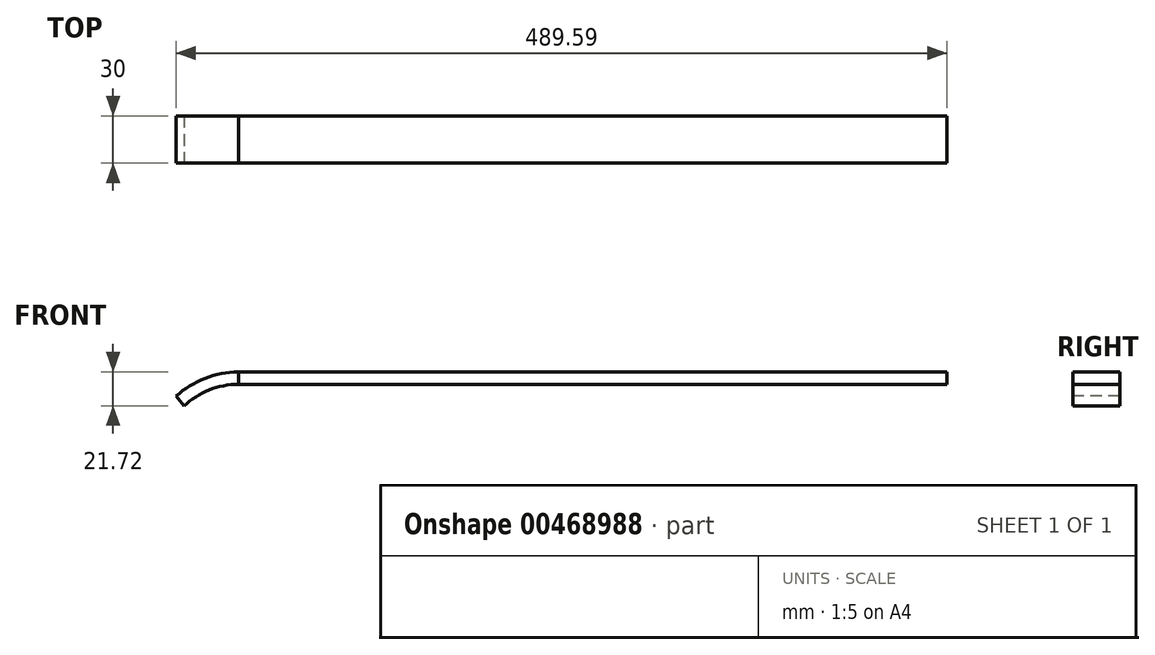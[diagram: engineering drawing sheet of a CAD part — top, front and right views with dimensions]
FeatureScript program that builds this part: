
annotation { "Feature Type Name" : "Feature", "Feature Type Description" : "" }
export const myFeature = defineFeature(function(context is Context, id is Id, definition is map)
    precondition{}
    {
        {
            var Q0;
            Q0=qCreatedBy(makeId("Top.planeOp"),FACE);
            var sketch = newSketch(context, id + "F0", { "sketchPlane" : qUnion([Q0])});
            skLineSegment(sketch, "E0.bottom", {"start": v(0, 0) * mm, "end": v(-450, 0) * mm});
            skLineSegment(sketch, "E0.top", {"start": v(0, -30) * mm, "end": v(-450, -30) * mm});
            skLineSegment(sketch, "E0.left", {"start": v(0, 0) * mm, "end": v(0, -30) * mm});
            skLineSegment(sketch, "E0.right", {"start": v(-450, 0) * mm, "end": v(-450, -30) * mm});
            skSolve(sketch);
        }
        {
            var Q0;
            Q0=makeQuery(id+"F0.imprint","IMPRINT",FACE,{"disambiguationData":[TD([[makeQuery(id+"F0.imprint","IMPRINT",EDGE,{"derivedFrom":sQuery(id+"F0.wireOp",EDGE,"E0.bottom")}),1.0]])]});
            extrude(context, id + "F1", {"entities" : qUnion([Q0]), "depth" : 8 * mm, "offsetDistance" : 25 * mm});
        }
        {
            var Q0;
            Q0=makeQuery(id+"F1.opExtrude","SWEPT_FACE",FACE,{"disambiguationData":[OSD([sQuery(id+"F0.wireOp",EDGE,"E0.top")])]});
            var sketch = newSketch(context, id + "F2", { "sketchPlane" : qUnion([Q0])});
            skArc(sketch, "E1", {"start": v(-450, 7.86) * mm, "mid": v(-471.2, 3.8) * mm, "end": v(-489.6, -7.5) * mm});
            skLineSegment(sketch, "E2", {"start": v(-450, 0) * mm, "end": v(-419.8, 0) * mm});
            skLineSegment(sketch, "E3", {"start": v(-484.53, -13.72) * mm, "end": v(-489.6, -7.5) * mm});
            skLineSegment(sketch, "E4", {"start": v(-450, 0) * mm, "end": v(-450, 8) * mm});
            skLineSegment(sketch, "E5", {"start": v(-450, 8) * mm, "end": v(-450, 0) * mm});
            skArc(sketch, "E6", {"start": v(-450, 0) * mm, "mid": v(-468.58, -3.55) * mm, "end": v(-484.53, -13.72) * mm});
            skSolve(sketch);
        }
        {
            var Q0;
            {var subQ0=sQuery(id+"F2.wireOp",EDGE,"E1");Q0=makeQuery(id+"F2.imprint","IMPRINT",FACE,{"disambiguationData":[TD([[makeQuery(id+"F2.imprint","IMPRINT",EDGE,{"derivedFrom":subQ0}),1.0]])]});}
            extrude(context, id + "F3", {"entities" : qUnion([Q0]), "oppositeDirection" : true, "depth" : 30 * mm});
        }
    });
